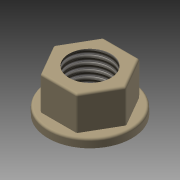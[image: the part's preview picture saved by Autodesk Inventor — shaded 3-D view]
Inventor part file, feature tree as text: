
AUTODESK INVENTOR PART (.ipt)
format: ipt  version: 2015 (Build 190159000, 159)  size: 134,656 bytes
history: native  units: mm
features: extrude x3, sketch x3, fillet x1, thread x1
ambient origin geometry x8: Origin, YZ Plane, XZ Plane, XY Plane, X Axis, Y Axis, Z Axis, Center Point
bodies: 实体1 (feature_tree)
feature tree (8):
  extrude  "拉伸1"  Depth=2.0mm TaperAngle=0.0deg
  extrude  "拉伸2"  Depth=15.0mm
  fillet  "圆角1"  Radius=8.0mm
  extrude  "拉伸3"  Depth=10.0mm
  thread  "螺纹1"  [1 undecoded]
  sketch  "草图1"  dims[d0=20.0mm d1=2.0mm d2=0.0mm]
  sketch  "草图2"  dims[d3=2.640688mm d4=15.0mm d5=8.0mm d6=0.0mm]
  sketch  "草图3"  dims[d7=0.5mm d8=10.0mm d9=8.0mm d10=0.0mm d11=10.0mm d12=0.0mm]
note: 1 required parameter value undecoded (feature->parameter linkage not recoverable at this tier; creation-order binding heuristic only, values carry confidence <= 0.55)
